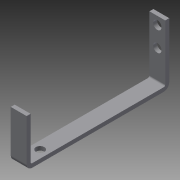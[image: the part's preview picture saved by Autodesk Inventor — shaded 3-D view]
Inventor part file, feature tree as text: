
AUTODESK INVENTOR PART (.ipt)
format: ipt  version: 2013 (Build 170138000, 138)  size: 129,536 bytes
history: native  units: in
note: dims shown in document units (in); Inventor stores cm internally (conversion verified against a paired STEP export)
features: sheet_metal_op x7, sketch x5, other x5, reference x2
ambient origin geometry x8: Origin, YZ Plane, XZ Plane, XY Plane, X Axis, Y Axis, Z Axis, Center Point
bodies: Solid1 (feature_tree)
feature tree (19):
  sheet_metal_op  "Face1"
  sheet_metal_op  "Flange1"
  sheet_metal_op  "Flange2"
  sketch  "Sketch1"  dims[d0=0.5in]
  other  "Plate1"
  sketch  "Sketch2"  dims[d1=1.75in]
  other  "Plate2"
  sheet_metal_op  "Bend1"
  sheet_metal_op  "Corner1"
  sketch  "Sketch3"  dims[d2=0.125in]
  reference  "Reference1"
  reference  "Reference2"
  sketch  "Sketch5"  dims[d3=0.125in]
  other  "Plate3"
  sheet_metal_op  "Bend2"
  sheet_metal_op  "Corner2"
  sketch  "Sketch6"  dims[d4=0.0625in d5=0.25in d6=0.125in d7=4.2723in d8=90.0deg d9=0.05in d10=0.5in d11=0.125in d12=0.125in d13=0.125in d14=0.0in d19=0.125in d20=0.0625in d21=0.25in d22=0.125in d23=1.5in d24=90.0deg d25=0.05in d26=0.5in d27=0.125in d28=0.125in d29=0.4417in d31=0.442in d32=0.266in d33=0.266in d34=0.125in d35=0.0in]
  other  "Cut1"
  other  "Cut3"
